# Revit family: Renzo Tile 300x300 Warning TGSI
name_source: partatom
category: Generic Models
units: mm (PartAtom-declared; Revit-internal decimal feet)

## family parameters
Always vertical = No
Can host rebar = No
Cut with Voids When Loaded = No
Host = Floor
Part Type = Normal
Room Calculation Point = No
Round Connector Dimension = Use Diameter
Shared = No

## types (8) — shared parameters
Description = Slip Resistance Classification: P5
Luminous Contrast Requirement (LCR): 30%
Manufacturer = Korb
URL = https://korb.au
zero-valued in all types: Default Elevation

## per-type parameters (varying)
| type | Assembly Code | Model | TGSI_Material | Type Comments |
| Renzo Tile 300x300 Orange - Integrated Warning | SKU: 123111 | Renzo® Tile 300x300 Black - Integrated Warning | Opaque Orange | Mean Dry Luminance (LRV): 1.91
Mean Wet Luminance (LRV): 1.89 |
| Renzo Tile 300x300 Black - Integrated Warning | SKU: 123111 | Renzo® Tile 300x300 Black - Integrated Warning | Opaque Black | Mean Dry Luminance (LRV): 1.91
Mean Wet Luminance (LRV): 1.89 |
| Renzo Tile 300x300 Charcoal - Integrated Warning | SKU: 123112 | Renzo® Tile 300x300 Charcoal - Integrated Warning | Opaque Charcoal | Mean Dry Luminance (LRV): 11.34
Mean Wet Luminance (LRV): 11.61 |
| Renzo Tile 300x300 Light Grey - Integrated Warning | SKU: 123113 | Renzo® Tile 300x300 Light Grey - Integrated Warning | Opaque  Light Grey | Mean Dry Luminance (LRV): 58.89
Mean Wet Luminance (LRV): 58.63 |
| Renzo Tile 300x300 White - Integrated Warning | SKU: 123114 | Renzo® Tile 300x300 White - Integrated Warning | Opaque  White | Mean Dry Luminance (LRV): 87.6
Mean Wet Luminance (LRV): 87.65 |
| Renzo Tile 300x300 Blue - Integrated Warning | SKU: 123115 | Renzo® Tile 300x300 Blue - Integrated Warning | Opaque  Blue | Mean Dry Luminance (LRV): 8.73
Mean Wet Luminance (LRV): 8.66 |
| Renzo Tile 300x300 Red - Integrated Warning | SKU: 123116 | Renzo® Tile 300x300 Red - Integrated Warning | Opaque  Red | Mean Dry Luminance (LRV): 16.26
Mean Wet Luminance (LRV): 15.85 |
| Renzo Tile 300x300 Yellow - Integrated Warning | SKU: 123118 | Renzo® Tile 300x300 Yellow - Integrated Warning | Opaque  Yellow | Mean Dry Luminance (LRV): 70.01
Mean Wet Luminance (LRV): 69.75 |

## geometry (parser evidence)
native form markers: Sweep x9
no freeform markers — native parametric forms only
